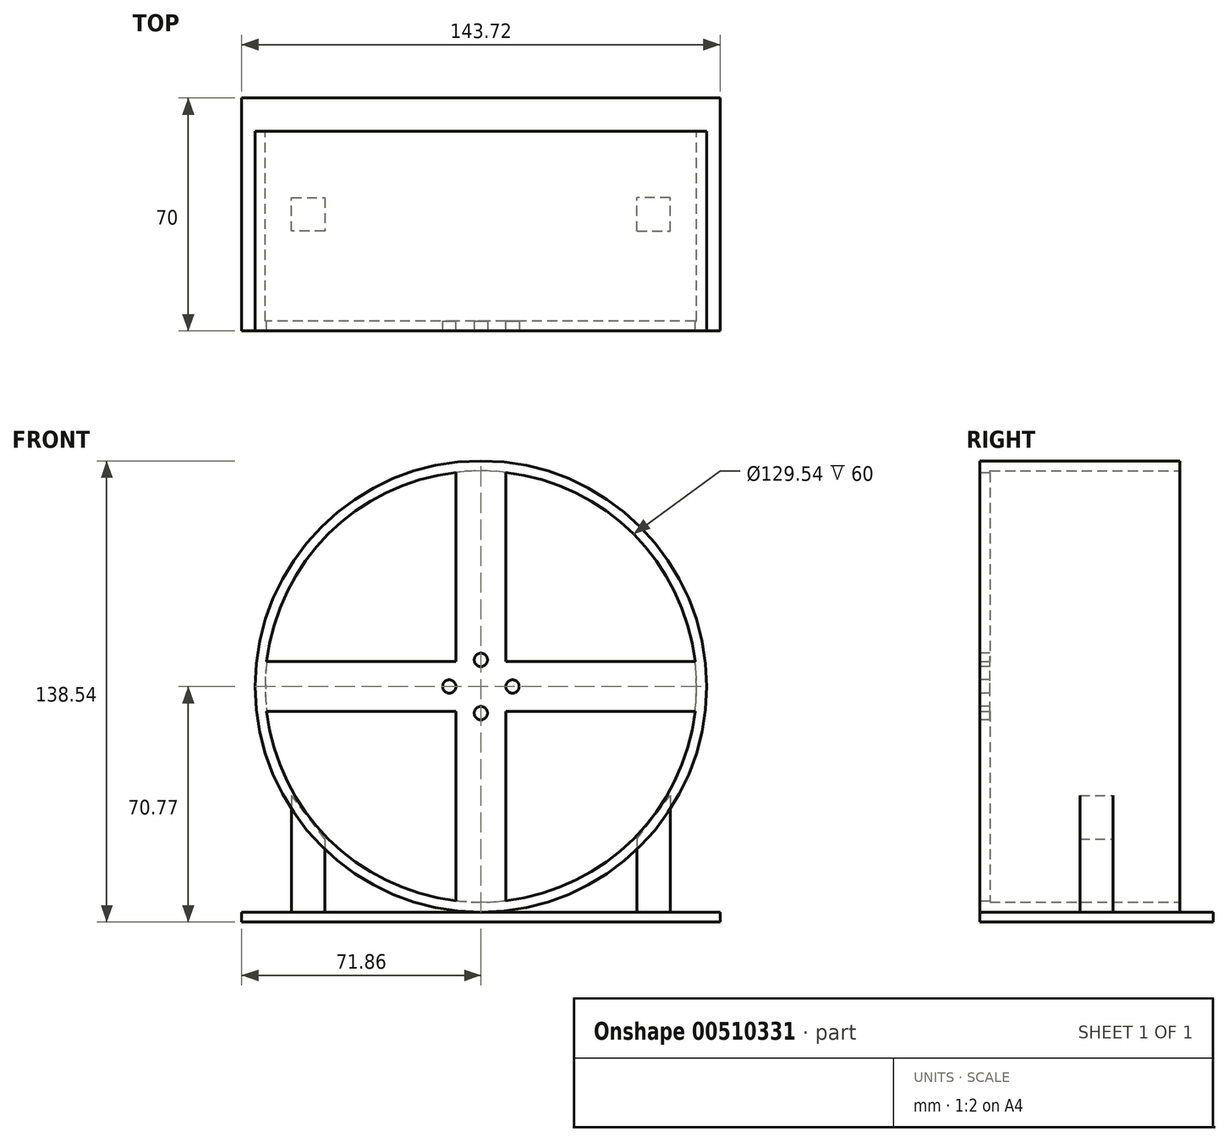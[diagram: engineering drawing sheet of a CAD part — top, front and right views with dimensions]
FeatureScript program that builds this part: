
annotation { "Feature Type Name" : "Feature", "Feature Type Description" : "" }
export const myFeature = defineFeature(function(context is Context, id is Id, definition is map)
    precondition{}
    {
        {
            var Q0;
            Q0=qCreatedBy(makeId("Front.planeOp"),FACE);
            var sketch = newSketch(context, id + "F0", { "sketchPlane" : qUnion([Q0])});
            skCircle(sketch, "E0", {"center": v(0, 0) * mm, "radius": 67.77 * mm});
            skSolve(sketch);
        }
        {
            var Q0;
            Q0=makeQuery(id+"F0.imprint","IMPRINT",FACE,{"disambiguationData":[TD([[makeQuery(id+"F0.imprint","IMPRINT",EDGE,{"derivedFrom":sQuery(id+"F0.wireOp",EDGE,"E0")}),1.0]])]});
            extrude(context, id + "F1", {"entities" : qUnion([Q0]), "depth" : 60 * mm, "offsetDistance" : 25 * mm});
        }
        {
            var Q0;
            Q0=makeQuery(id+"F1.opExtrude","CAP_FACE",FACE,{"disambiguationData":[OSD([sQuery(id+"F0.wireOp",EDGE,"E0")])],"isStart":false});
            var Q1;
            Q1=makeQuery(id+"F1.opExtrude","CAP_FACE",FACE,{"disambiguationData":[OSD([sQuery(id+"F0.wireOp",EDGE,"E0")])],"isStart":true});
            shell(context, id + "F2", {"entities" : qUnion([Q0, Q1]), "thickness" : 3 * mm});
        }
        {
            var Q0;
            Q0=qCreatedBy(makeId("Top.planeOp"),FACE);
            cPlane(context, id + "F3", {"entities" : qUnion([Q0]), "cplaneType" : CPlaneType.OFFSET, "offset" : 67.77 * mm, "oppositeDirection" : true, "width" : 150 * mm, "height" : 150 * mm});
        }
        {
            var Q0;
            Q0=qCreatedBy(id+"F3.planeOp",FACE);
            var sketch = newSketch(context, id + "F4", { "sketchPlane" : qUnion([Q0])});
            skLineSegment(sketch, "E1.bottom", {"start": v(-71.86, 10) * mm, "end": v(71.86, 10) * mm});
            skLineSegment(sketch, "E1.top", {"start": v(-71.86, -60) * mm, "end": v(71.86, -60) * mm});
            skLineSegment(sketch, "E1.left", {"start": v(-71.86, 10) * mm, "end": v(-71.86, -60) * mm});
            skLineSegment(sketch, "E1.right", {"start": v(71.86, 10) * mm, "end": v(71.86, -60) * mm});
            skSolve(sketch);
        }
        {
            var Q0;
            Q0 = qSketchRegion(id + "F4", true);
            extrude(context, id + "F5", {"entities" : qUnion([Q0]), "operationType" : NewBodyOperationType.ADD, "oppositeDirection" : true, "depth" : 3 * mm, "offsetDistance" : 25 * mm});
        }
        {
            var Q0;
            Q0=makeQuery(id+"F5.opExtrude","CAP_FACE",FACE,{"disambiguationData":[OSD([sQuery(id+"F4.wireOp",EDGE,"E1.bottom"),sQuery(id+"F4.wireOp",EDGE,"E1.top"),sQuery(id+"F4.wireOp",EDGE,"E1.left"),sQuery(id+"F4.wireOp",EDGE,"E1.right")])],"isStart":true});
            var sketch = newSketch(context, id + "F6", { "sketchPlane" : qUnion([Q0])});
            skLineSegment(sketch, "E2.bottom", {"start": v(-56.86, -30) * mm, "end": v(-46.86, -30) * mm});
            skLineSegment(sketch, "E2.top", {"start": v(-56.86, -20) * mm, "end": v(-46.86, -20) * mm});
            skLineSegment(sketch, "E2.left", {"start": v(-56.86, -30) * mm, "end": v(-56.86, -20) * mm});
            skLineSegment(sketch, "E2.right", {"start": v(-46.86, -30) * mm, "end": v(-46.86, -20) * mm});
            skLineSegment(sketch, "E3.bottom", {"start": v(46.86, -30) * mm, "end": v(56.86, -30) * mm});
            skLineSegment(sketch, "E3.top", {"start": v(46.86, -20) * mm, "end": v(56.86, -20) * mm});
            skLineSegment(sketch, "E3.left", {"start": v(46.86, -30) * mm, "end": v(46.86, -20) * mm});
            skLineSegment(sketch, "E3.right", {"start": v(56.86, -30) * mm, "end": v(56.86, -20) * mm});
            skSolve(sketch);
        }
        {
            var Q0;
            Q0 = qSketchRegion(id + "F6", true);
            extrude(context, id + "F7", {"entities" : qUnion([Q0]), "depth" : 35 * mm, "offsetDistance" : 25 * mm});
        }
        {
            var Q0;
            Q0=makeQuery(id+"F7.opExtrude","CAP_EDGE",EDGE,{"disambiguationData":[OSD([sQuery(id+"F6.wireOp",EDGE,"E2.right")])],"isStart":false});
            chamfer(context, id + "F8", {"entities" : qUnion([Q0]), "chamferType" : ChamferType.TWO_OFFSETS, "width1" : 10 * mm, "oppositeDirection" : false, "width2" : 13 * mm, "tangentPropagation" : true});
        }
        {
            var Q0;
            Q0=makeQuery(id+"F7.opExtrude","CAP_EDGE",EDGE,{"disambiguationData":[OSD([sQuery(id+"F6.wireOp",EDGE,"E3.left")])],"isStart":false});
            chamfer(context, id + "F9", {"entities" : qUnion([Q0]), "chamferType" : ChamferType.TWO_OFFSETS, "width1" : 13 * mm, "oppositeDirection" : false, "width2" : 10 * mm, "tangentPropagation" : true});
        }
        {
            var Q0;
            Q0=makeQuery(id+"F1.opExtrude","CAP_FACE",FACE,{"disambiguationData":[OSD([sQuery(id+"F0.wireOp",EDGE,"E0")])],"isStart":false});
            var sketch = newSketch(context, id + "F10", { "sketchPlane" : qUnion([Q0])});
            skLineSegment(sketch, "E4.bottom", {"start": v(7.5, 65) * mm, "end": v(-7.5, 65) * mm});
            skLineSegment(sketch, "E4.top", {"start": v(7.5, -65) * mm, "end": v(-7.5, -65) * mm});
            skLineSegment(sketch, "E4.left", {"start": v(7.5, 65) * mm, "end": v(7.5, -65) * mm});
            skLineSegment(sketch, "E4.right", {"start": v(-7.5, 65) * mm, "end": v(-7.5, -65) * mm});
            skPoint(sketch, "E4.middle", {"position": v(0, 0) * mm});
            skLineSegment(sketch, "E5.bottom", {"start": v(65, 7.5) * mm, "end": v(-65, 7.5) * mm});
            skLineSegment(sketch, "E5.top", {"start": v(65, -7.5) * mm, "end": v(-65, -7.5) * mm});
            skLineSegment(sketch, "E5.left", {"start": v(65, 7.5) * mm, "end": v(65, -7.5) * mm});
            skLineSegment(sketch, "E5.right", {"start": v(-65, 7.5) * mm, "end": v(-65, -7.5) * mm});
            skSolve(sketch);
        }
        {
            var Q0;
            Q0 = qSketchRegion(id + "F10", true);
            extrude(context, id + "F11", {"entities" : qUnion([Q0]), "operationType" : NewBodyOperationType.ADD, "oppositeDirection" : true, "depth" : 3 * mm, "offsetDistance" : 25 * mm});
        }
        {
            var Q0;
            Q0=makeQuery(id+"F11.boolean.opBoolean","MERGE",FACE,{"derivedFrom":[makeQuery(id+"F1.opExtrude","CAP_FACE",FACE,{"disambiguationData":[OSD([sQuery(id+"F0.wireOp",EDGE,"E0")])],"isStart":false}),makeQuery(id+"F11.opExtrude","CAP_FACE",FACE,{"disambiguationData":[OSD([sQuery(id+"F10.wireOp",EDGE,"E4.bottom"),sQuery(id+"F10.wireOp",EDGE,"E4.top"),sQuery(id+"F10.wireOp",EDGE,"E4.left"),sQuery(id+"F10.wireOp",EDGE,"E4.right"),sQuery(id+"F10.wireOp",EDGE,"E5.bottom"),sQuery(id+"F10.wireOp",EDGE,"E5.top"),sQuery(id+"F10.wireOp",EDGE,"E5.left"),sQuery(id+"F10.wireOp",EDGE,"E5.right")])],"isStart":true})]});
            var sketch = newSketch(context, id + "F12", { "sketchPlane" : qUnion([Q0])});
            skCircle(sketch, "E6", {"center": v(0, 8) * mm, "radius": 2 * mm});
            skCircle(sketch, "E7", {"center": v(9.5, 0) * mm, "radius": 2 * mm});
            skCircle(sketch, "E8", {"center": v(-9.5, 0) * mm, "radius": 2 * mm});
            skCircle(sketch, "E9", {"center": v(0, -8) * mm, "radius": 2 * mm});
            skSolve(sketch);
        }
        {
            var Q0;
            Q0 = qSketchRegion(id + "F12", true);
            extrude(context, id + "F13", {"entities" : qUnion([Q0]), "operationType" : NewBodyOperationType.REMOVE, "oppositeDirection" : true, "depth" : 3 * mm, "offsetDistance" : 25 * mm});
        }
    });
